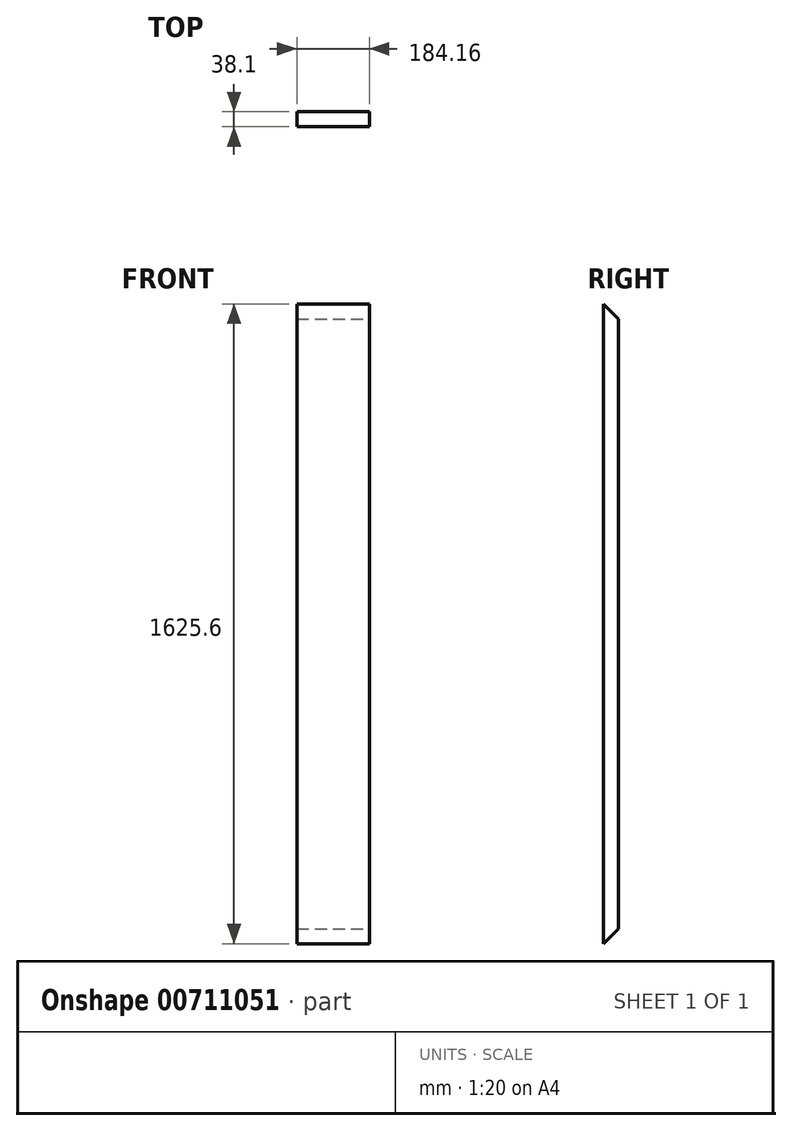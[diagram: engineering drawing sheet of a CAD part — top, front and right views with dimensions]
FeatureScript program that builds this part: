
annotation { "Feature Type Name" : "Feature", "Feature Type Description" : "" }
export const myFeature = defineFeature(function(context is Context, id is Id, definition is map)
    precondition{}
    {
        {
            var Q0;
            Q0=qCreatedBy(makeId("Top.planeOp"),FACE);
            var sketch = newSketch(context, id + "F0", { "sketchPlane" : qUnion([Q0])});
            skLineSegment(sketch, "E0.bottom", {"start": v(92.08, 19.05) * mm, "end": v(-92.08, 19.05) * mm});
            skLineSegment(sketch, "E0.top", {"start": v(92.08, -19.05) * mm, "end": v(-92.07, -19.05) * mm});
            skLineSegment(sketch, "E0.left", {"start": v(92.08, 19.05) * mm, "end": v(92.08, -19.05) * mm});
            skLineSegment(sketch, "E0.right", {"start": v(-92.08, 19.05) * mm, "end": v(-92.08, -19.05) * mm});
            skPoint(sketch, "E0.middle", {"position": v(0, 0) * mm});
            skSolve(sketch);
        }
        {
            var Q0;
            Q0=makeQuery(id+"F0.imprint","IMPRINT",FACE,{"disambiguationData":[TD([[makeQuery(id+"F0.imprint","IMPRINT",EDGE,{"derivedFrom":sQuery(id+"F0.wireOp",EDGE,"E0.bottom")}),1.0]])]});
            extrude(context, id + "F1", {"entities" : qUnion([Q0]), "depth" : 1625.6 * mm, "offsetDistance" : 25.4 * mm});
        }
        {
            var Q0;
            Q0=makeQuery(id+"F1.opExtrude","SWEPT_FACE",FACE,{"disambiguationData":[OSD([sQuery(id+"F0.wireOp",EDGE,"E0.left")])]});
            var sketch = newSketch(context, id + "F2", { "sketchPlane" : qUnion([Q0])});
            skLineSegment(sketch, "E1", {"start": v(-19.05, 1625.6) * mm, "end": v(19.05, 1587.5) * mm});
            skLineSegment(sketch, "E2", {"start": v(-19.05, 1625.6) * mm, "end": v(19.05, 1625.6) * mm});
            skLineSegment(sketch, "E3", {"start": v(19.05, 1625.6) * mm, "end": v(19.05, 1587.5) * mm});
            skLineSegment(sketch, "E4", {"start": v(-19.05, 0) * mm, "end": v(19.05, 38.1) * mm});
            skLineSegment(sketch, "E5", {"start": v(-19.05, 0) * mm, "end": v(19.05, 0) * mm});
            skLineSegment(sketch, "E6", {"start": v(19.05, 0) * mm, "end": v(19.05, 38.1) * mm});
            skSolve(sketch);
        }
        {
            var Q0;
            Q0=qSketchRegion(id+"F2",true);
            extrude(context, id + "F3", {"entities" : qUnion([Q0]), "operationType" : NewBodyOperationType.REMOVE, "oppositeDirection" : true, "depth" : 190.5 * mm, "offsetDistance" : 25.4 * mm});
        }
    });
